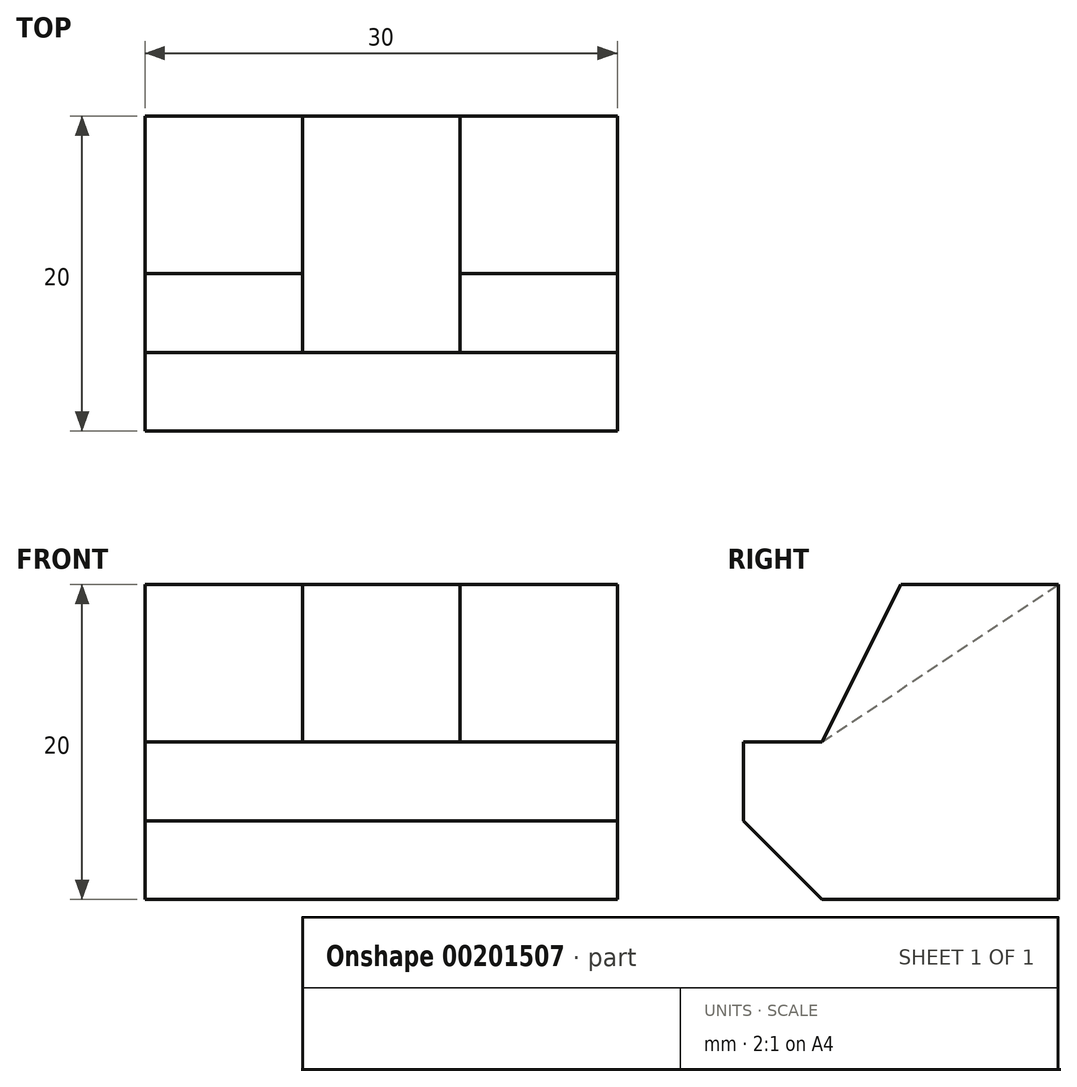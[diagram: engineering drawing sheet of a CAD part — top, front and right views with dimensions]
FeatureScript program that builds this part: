
annotation { "Feature Type Name" : "Feature", "Feature Type Description" : "" }
export const myFeature = defineFeature(function(context is Context, id is Id, definition is map)
    precondition{}
    {
        {
            var Q0;
            Q0=qCreatedBy(makeId("Right.planeOp"),FACE);
            var sketch = newSketch(context, id + "F0", { "sketchPlane" : qUnion([Q0])});
            skLineSegment(sketch, "E0", {"start": v(0, 0) * mm, "end": v(0, 20) * mm});
            skLineSegment(sketch, "E1", {"start": v(0, 20) * mm, "end": v(-10, 20) * mm});
            skLineSegment(sketch, "E2", {"start": v(-10, 20) * mm, "end": v(-15, 10) * mm});
            skLineSegment(sketch, "E3", {"start": v(-15, 10) * mm, "end": v(-20, 10) * mm});
            skLineSegment(sketch, "E4", {"start": v(-20, 10) * mm, "end": v(-20, 0) * mm});
            skLineSegment(sketch, "E5", {"start": v(-20, 0) * mm, "end": v(0, 0) * mm});
            skLineSegment(sketch, "E6", {"start": v(-15, 10) * mm, "end": v(0, 20) * mm});
            skSolve(sketch);
        }
        {
            var Q0;
            Q0=qSketchRegion(id+"F0",true);
            extrude(context, id + "F1", {"entities" : qUnion([Q0]), "endBound" : BoundingType.SYMMETRIC, "depth" : 30 * mm});
        }
        {
            var Q0;
            Q0=makeQuery(id+"F0.imprint","IMPRINT",FACE,{"disambiguationData":[TD([[makeQuery(id+"F0.imprint","IMPRINT",EDGE,{"derivedFrom":sQuery(id+"F0.wireOp",EDGE,"E1")}),1.0]])]});
            extrude(context, id + "F2", {"entities" : qUnion([Q0]), "operationType" : NewBodyOperationType.REMOVE, "endBound" : BoundingType.SYMMETRIC, "oppositeDirection" : true, "depth" : 10 * mm});
        }
        {
            var Q0;
            Q0=makeQuery(id+"F1.opExtrude","SWEPT_EDGE",EDGE,{"disambiguationData":[OSD([sQuery(id+"F0.wireOp",EDGE,"E4"),sQuery(id+"F0.wireOp",EDGE,"E5")])]});
            chamfer(context, id + "F3", {"entities" : qUnion([Q0]), "width" : 5 * mm, "tangentPropagation" : true});
        }
    });
